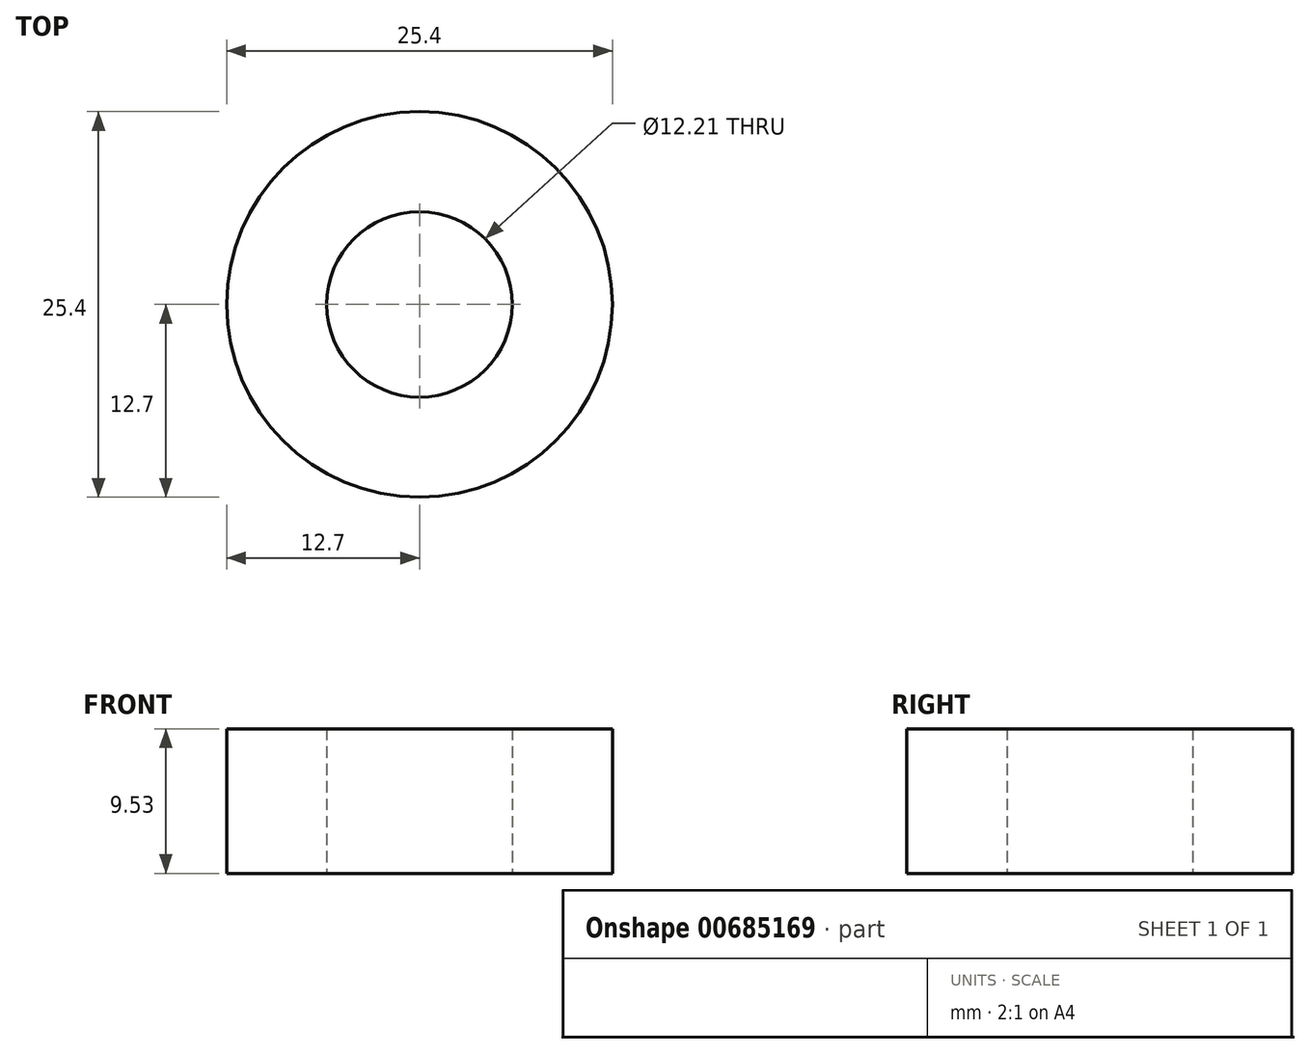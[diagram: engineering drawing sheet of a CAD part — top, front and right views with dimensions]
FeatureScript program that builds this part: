
annotation { "Feature Type Name" : "Feature", "Feature Type Description" : "" }
export const myFeature = defineFeature(function(context is Context, id is Id, definition is map)
    precondition{}
    {
        {
            var Q0;
            Q0=qCreatedBy(makeId("Top.planeOp"),FACE);
            var sketch = newSketch(context, id + "F0", { "sketchPlane" : qUnion([Q0])});
            skCircle(sketch, "E0", {"center": v(0, 0) * mm, "radius": 6.1 * mm});
            skCircle(sketch, "E1", {"center": v(0, 0) * mm, "radius": 12.7 * mm});
            skSolve(sketch);
        }
        {
            var Q0;
            Q0=qSketchRegion(id+"F0",true);
            extrude(context, id + "F1", {"entities" : qUnion([Q0]), "depth" : 9.52 * mm, "offsetDistance" : 25.4 * mm});
        }
    });
